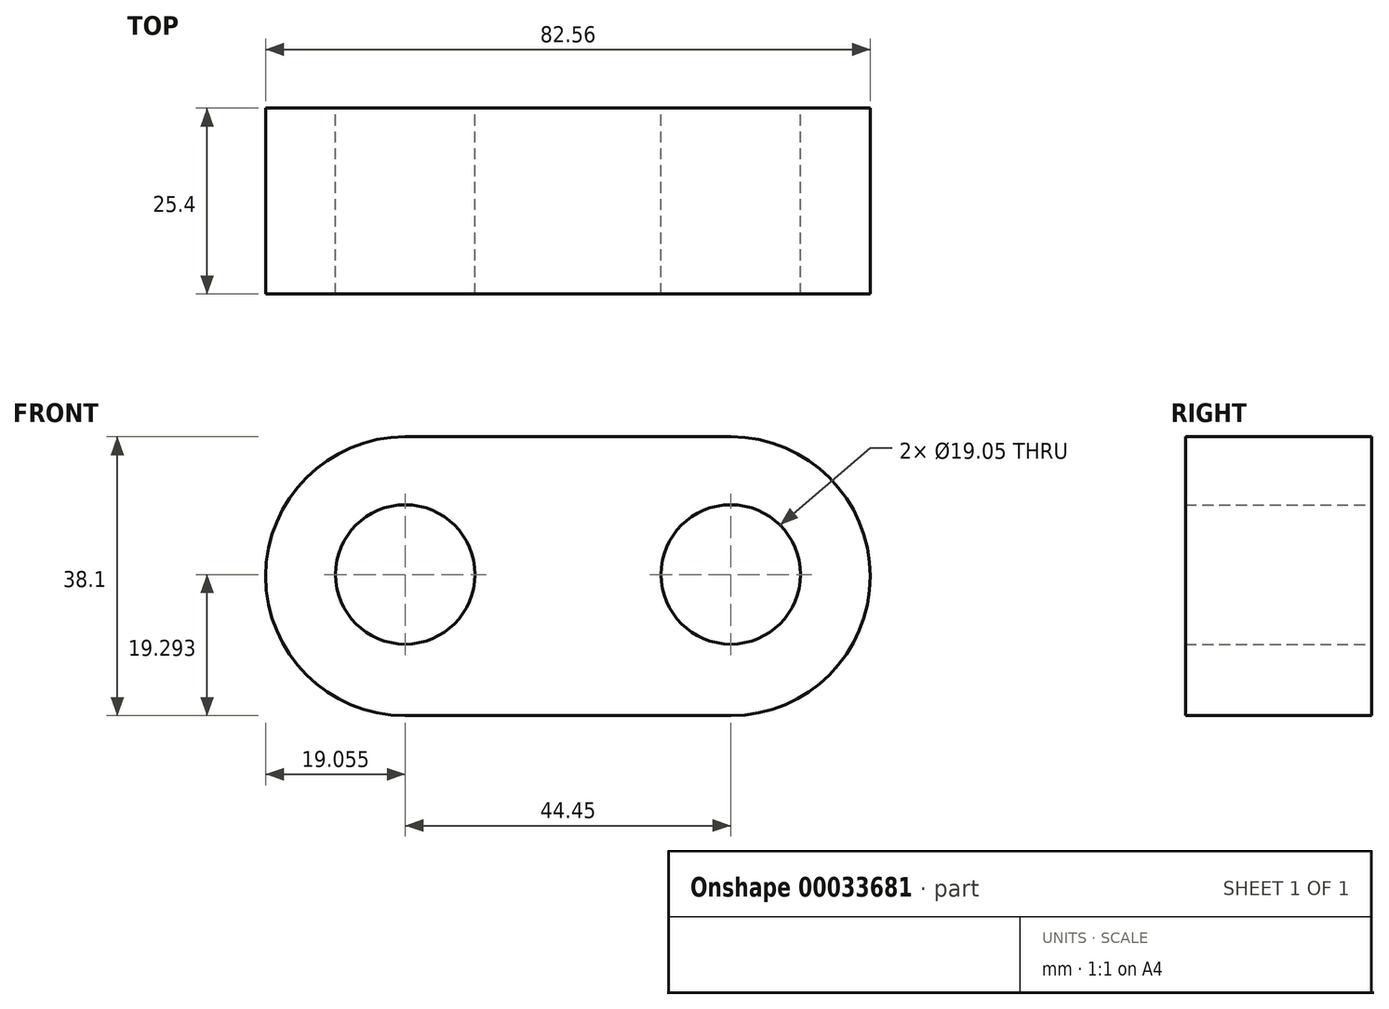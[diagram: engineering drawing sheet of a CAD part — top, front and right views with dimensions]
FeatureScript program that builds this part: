
annotation { "Feature Type Name" : "Feature", "Feature Type Description" : "" }
export const myFeature = defineFeature(function(context is Context, id is Id, definition is map)
    precondition{}
    {
        {
            var Q0;
            Q0=qCreatedBy(makeId("Front.planeOp"),FACE);
            var sketch = newSketch(context, id + "F0", { "sketchPlane" : qUnion([Q0])});
            skLineSegment(sketch, "E0.bottom", {"start": v(-22.23, 18.93) * mm, "end": v(22.23, 18.93) * mm});
            skLineSegment(sketch, "E0.top", {"start": v(-22.23, -19.17) * mm, "end": v(22.23, -19.17) * mm});
            skLineSegment(sketch, "E0.left", {"start": v(-22.22, 18.93) * mm, "end": v(-22.22, -19.17) * mm});
            skLineSegment(sketch, "E0.right", {"start": v(22.23, 18.93) * mm, "end": v(22.23, -19.17) * mm});
            skLineSegment(sketch, "E1.bottom", {"start": v(-22.23, 9.65) * mm, "end": v(22.23, 9.65) * mm});
            skLineSegment(sketch, "E1.top", {"start": v(-22.22, -9.4) * mm, "end": v(22.23, -9.4) * mm});
            skLineSegment(sketch, "E1.left", {"start": v(-22.22, 9.65) * mm, "end": v(-22.22, -9.4) * mm});
            skLineSegment(sketch, "E1.right", {"start": v(22.23, 9.65) * mm, "end": v(22.23, -9.4) * mm});
            skArc(sketch, "E2", {"start": v(-22.23, 18.93) * mm, "mid": v(-41.28, -0.12) * mm, "end": v(-22.23, -19.17) * mm});
            skArc(sketch, "E3", {"start": v(22.23, -19.17) * mm, "mid": v(41.28, -0.12) * mm, "end": v(22.23, 18.93) * mm});
            skArc(sketch, "E4", {"start": v(-22.23, 9.65) * mm, "mid": v(-31.75, 0.12) * mm, "end": v(-22.22, -9.4) * mm});
            skArc(sketch, "E5", {"start": v(22.23, -9.4) * mm, "mid": v(31.75, 0.12) * mm, "end": v(22.23, 9.65) * mm});
            skCircle(sketch, "E6", {"center": v(-22.22, 0.12) * mm, "radius": 9.53 * mm});
            skCircle(sketch, "E7", {"center": v(22.23, 0.12) * mm, "radius": 9.53 * mm});
            skSolve(sketch);
        }
        {
            var Q0;
            {var subQ5=sQuery(id+"F0.wireOp",EDGE,"E3");Q0=makeQuery(id+"F0.imprint","IMPRINT",FACE,{"disambiguationData":[TD([[makeQuery(id+"F0.imprint","IMPRINT",EDGE,{"derivedFrom":subQ5}),1.0]])]});}
            var Q1;
            {var subQ2=sQuery(id+"F0.wireOp",EDGE,"E0.bottom");Q1=makeQuery(id+"F0.imprint","IMPRINT",FACE,{"disambiguationData":[TD([[makeQuery(id+"F0.imprint","IMPRINT",EDGE,{"derivedFrom":subQ2}),-1.0]])]});}
            var Q2;
            {var subQ2=sQuery(id+"F0.wireOp",EDGE,"E0.top");Q2=makeQuery(id+"F0.imprint","IMPRINT",FACE,{"disambiguationData":[TD([[makeQuery(id+"F0.imprint","IMPRINT",EDGE,{"derivedFrom":subQ2}),1.0]])]});}
            var Q3;
            {var subQ0=sQuery(id+"F0.wireOp",EDGE,"E2");Q3=makeQuery(id+"F0.imprint","IMPRINT",FACE,{"disambiguationData":[TD([[makeQuery(id+"F0.imprint","IMPRINT",EDGE,{"derivedFrom":subQ0}),1.0]])]});}
            var Q4;
            {var subQ4=sQuery(id+"F0.wireOp",EDGE,"E1.bottom");Q4=makeQuery(id+"F0.imprint","IMPRINT",FACE,{"disambiguationData":[TD([[makeQuery(id+"F0.imprint","IMPRINT",EDGE,{"derivedFrom":subQ4}),-1.0]])]});}
            extrude(context, id + "F1", {"entities" : qUnion([Q0, Q1, Q2, Q3, Q4]), "depth" : 25.4 * mm});
        }
    });
